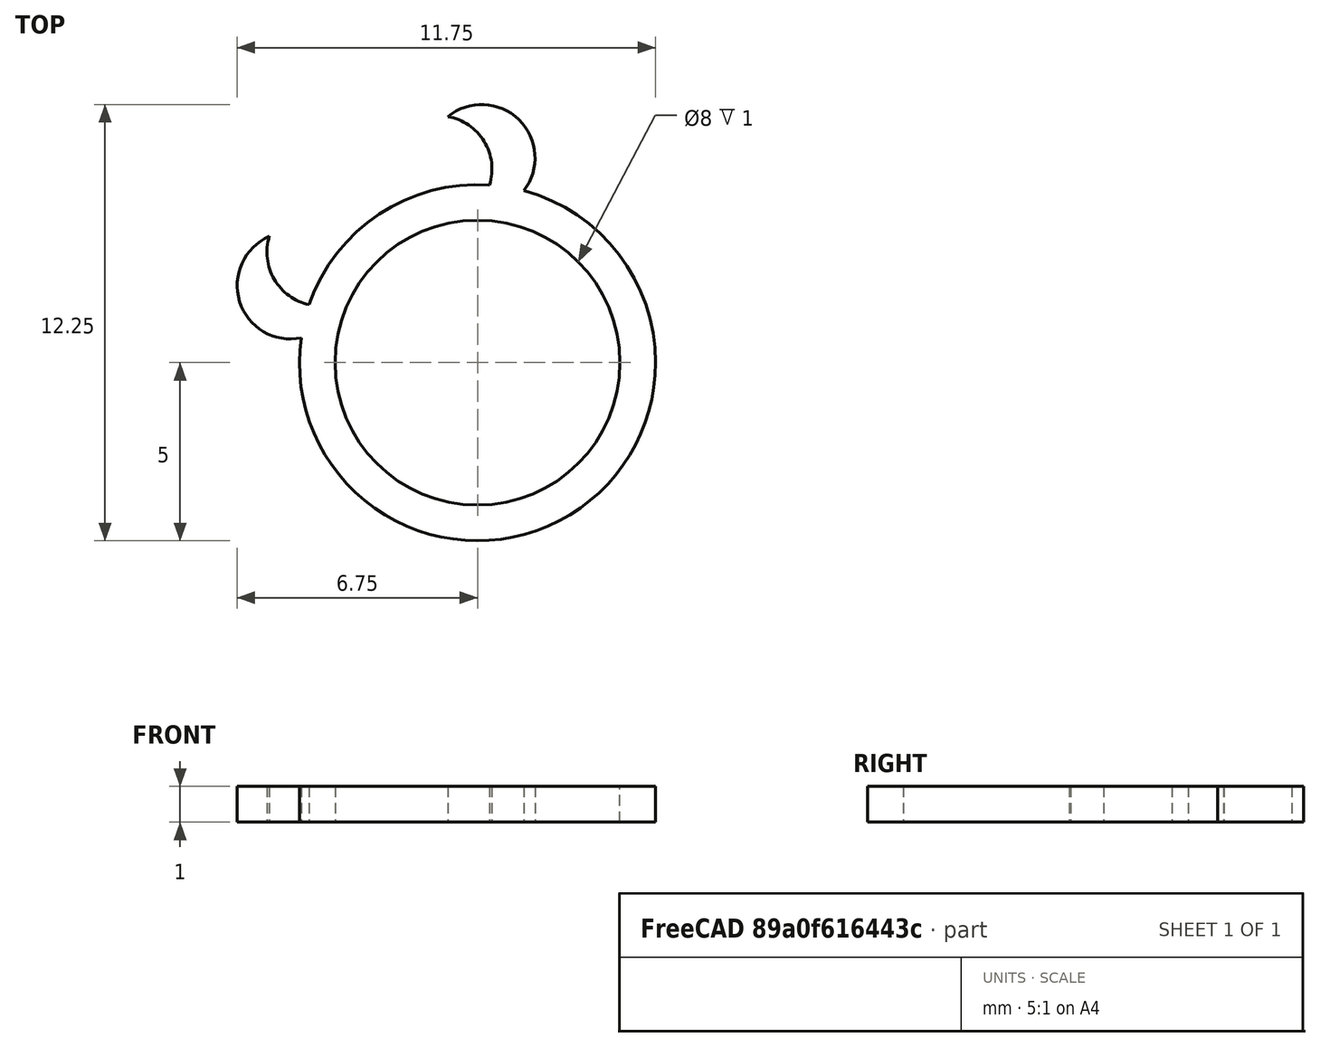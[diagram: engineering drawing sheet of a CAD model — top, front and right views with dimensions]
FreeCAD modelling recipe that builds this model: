
FCSTD DOCUMENT  (FreeCAD 1.0R38806 (Git))
Label: anillo_diablillo
License: All rights reserved
LicenseURL: https://en.wikipedia.org/wiki/All_rights_reserved
objects: Part::Cylinder×4, Part::Cut×2, Part::Mirroring×1, Part::MultiFuse×1
note: 8 computed .brp shape members not serialized (recipe doc carries the construction recipe); baked Part::Feature solids carry a one-line shape summary decoded from their .brp

FEATURE [Part::Cylinder] Cylinder
  Angle = 360
  AttacherType = Attacher::AttachEngine3D
  FirstAngle = 0
  Height = 1
  Radius = 5
  SecondAngle = 0
FEATURE [Part::Cylinder] Cylinder001
  Angle = 360
  AttacherType = Attacher::AttachEngine3D
  FirstAngle = 0
  Height = 10
  Placement = pos=(0,0,-5) rot=(0,0,1;0rad)
  Radius = 4
  SecondAngle = 0
FEATURE [Part::Cut] Cut
  Base = -> Cylinder
  Refine = true
  Tool = -> Cylinder001
FEATURE [Part::Cylinder] Cylinder002
  Angle = 360
  AttacherType = Attacher::AttachEngine3D
  FirstAngle = 0
  Height = 1
  Placement = pos=(-5.5,2,0) rot=(0,0,1;0rad)
  Radius = 1.5
  SecondAngle = 0
FEATURE [Part::Cylinder] Cylinder004
  Angle = 360
  AttacherType = Attacher::AttachEngine3D
  FirstAngle = 0
  Height = 1
  Placement = pos=(-5.5,3.25,0) rot=(0,0,1;0rad)
  Radius = 1.5
  SecondAngle = 0
FEATURE [Part::Cut] Cut001
  Base = -> Cylinder002
  Placement = pos=(-2.5,-3,0) rot=(0,0,1;-0.733038rad)
  Refine = true
  Tool = -> Cylinder004
FEATURE [Part::Mirroring] Mirror  label="Cut001 (mirrored)"
  Base = (-5.41632,1.98072,0)
  Normal = (0.964501,0.264078,0)
  Placement = pos=(6,7,0) rot=(0,0,1;0.558505rad)
  Source = -> Cut001
FEATURE [Part::MultiFuse] Fusion
  Refine = true
  Shapes = -> [Cut001,Mirror,Cut]
